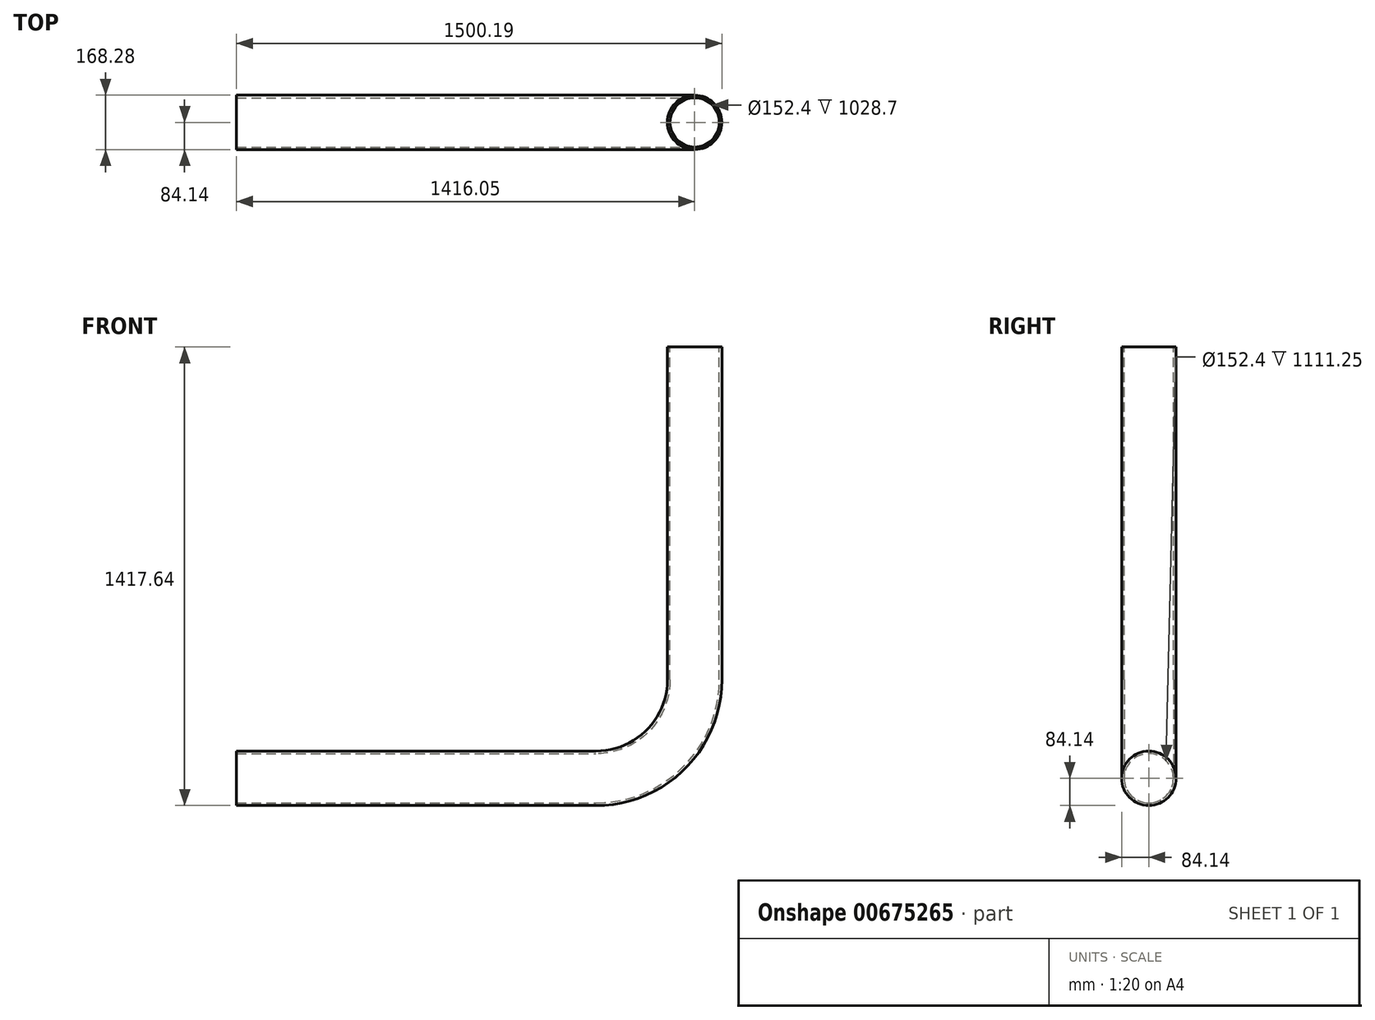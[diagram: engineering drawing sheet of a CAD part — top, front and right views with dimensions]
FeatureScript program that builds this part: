
annotation { "Feature Type Name" : "Feature", "Feature Type Description" : "" }
export const myFeature = defineFeature(function(context is Context, id is Id, definition is map)
    precondition{}
    {
        {
            var Q0;
            Q0=qCreatedBy(makeId("Front.planeOp"),FACE);
            var sketch = newSketch(context, id + "F0", { "sketchPlane" : qUnion([Q0])});
            skLineSegment(sketch, "E0", {"start": v(-304.8, 0) * mm, "end": v(-1416.05, 0) * mm});
            skLineSegment(sketch, "E1", {"start": v(0, 304.8) * mm, "end": v(0, 1333.5) * mm});
            skArc(sketch, "E2", {"start": v(-304.8, 0) * mm, "mid": v(-89.27, 89.27) * mm, "end": v(0, 304.8) * mm});
            skPoint(sketch, "E3.orphan", {"position": v(0, 0) * mm});
            skSolve(sketch);
        }
        {
            var Q0;
            Q0=qCreatedBy(makeId("Right.planeOp"),FACE);
            cPlane(context, id + "F1", {"entities" : qUnion([Q0]), "cplaneType" : CPlaneType.OFFSET, "offset" : 1416.05 * mm, "oppositeDirection" : true, "width" : 152.4 * mm, "height" : 152.4 * mm});
        }
        {
            var Q0;
            Q0=qCreatedBy(id+"F1.planeOp",FACE);
            var sketch = newSketch(context, id + "F2", { "sketchPlane" : qUnion([Q0])});
            skCircle(sketch, "E4", {"center": v(0, 0) * mm, "radius": 84.14 * mm});
            skCircle(sketch, "E5", {"center": v(0, 0) * mm, "radius": 76.2 * mm});
            skSolve(sketch);
        }
        {
            var Q0;
            Q0=makeQuery(id+"F2.imprint","IMPRINT",FACE,{"disambiguationData":[TD([[makeQuery(id+"F2.imprint","IMPRINT",EDGE,{"derivedFrom":sQuery(id+"F2.wireOp",EDGE,"E4")}),1.0]])]});
            var Q1;
            Q1=sQuery(id+"F0.wireOp",EDGE,"E0");
            var Q2;
            Q2=sQuery(id+"F0.wireOp",EDGE,"E2");
            var Q3;
            Q3=sQuery(id+"F0.wireOp",EDGE,"E1");
            sweep(context, id + "F3", {"profiles" : qUnion([Q0]), "path" : qUnion([Q1, Q2, Q3])});
        }
    });
